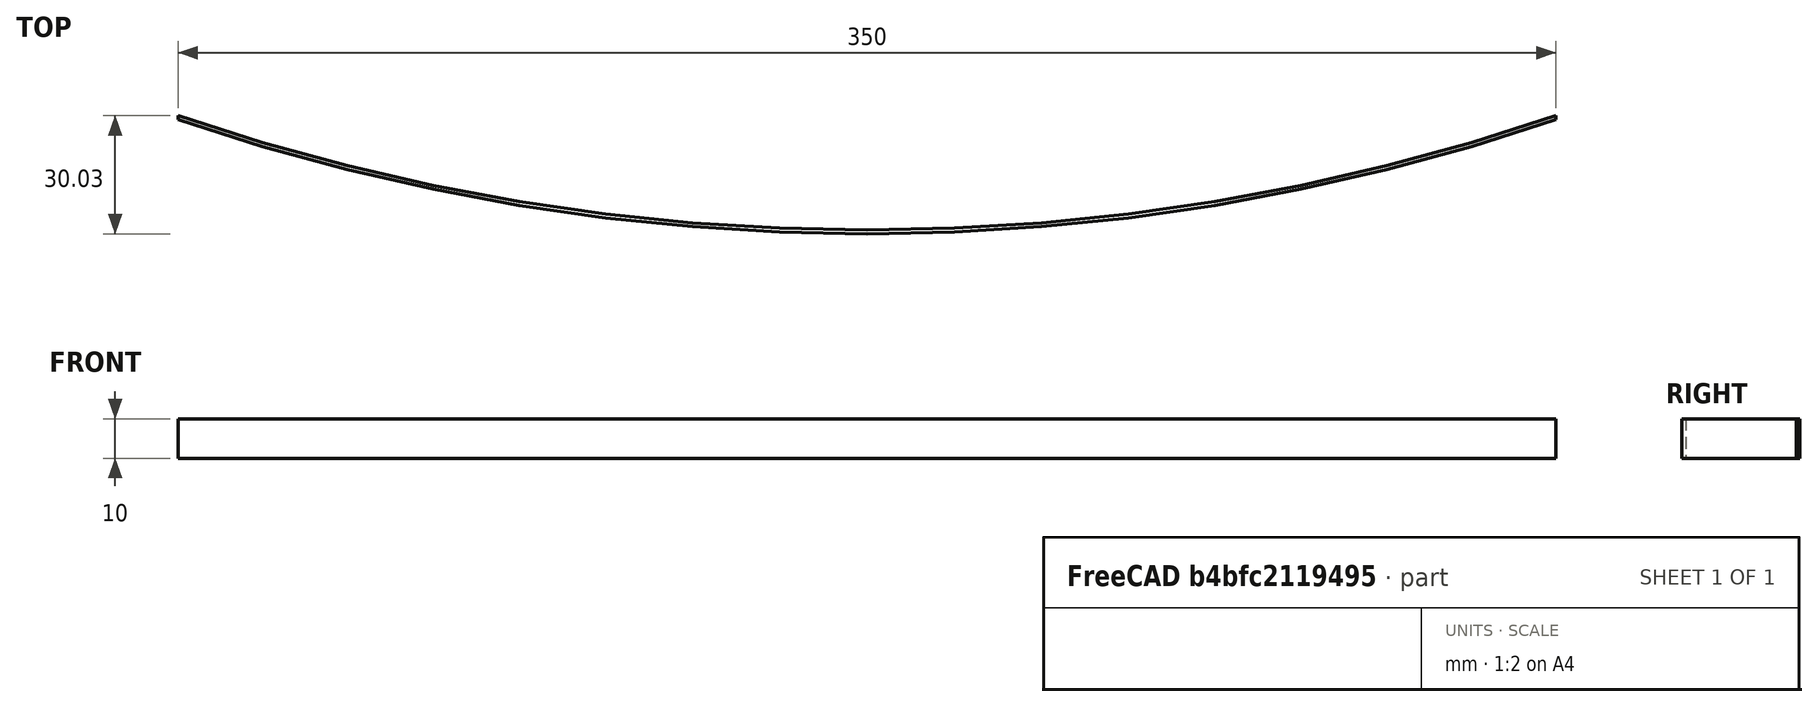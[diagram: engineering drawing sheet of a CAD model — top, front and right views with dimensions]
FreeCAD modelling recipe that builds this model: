
FCSTD DOCUMENT  (FreeCAD 0.19R24276 (Git))
Label: Strip_1
License: All rights reserved
LicenseURL: http://en.wikipedia.org/wiki/All_rights_reserved
objects: Sketcher::SketchObject×1, PartDesign::Pad×1, PartDesign::Body×1
note: 4 computed .brp shape members not serialized (recipe doc carries the construction recipe); baked Part::Feature solids carry a one-line shape summary decoded from their .brp

FEATURE [Sketcher::SketchObject] Sketch
  FullyConstrained = false
  MapMode = 5
  Support = -> [XY_Plane]
  sketch-geometry (4):
    g0: ArcOfCircle CenterX=175 CenterY=512.476 CenterZ=0 NormalX=0 NormalY=0 NormalZ=1 AngleXU=0 Radius=541.532 StartAngle=4.38332 EndAngle=5.04145
    g1: ArcOfCircle CenterX=175 CenterY=511.991 CenterZ=0 NormalX=0 NormalY=0 NormalZ=1 AngleXU=0 Radius=542.019 StartAngle=4.38363 EndAngle=5.04115
    g2: LineSegment StartX=350 StartY=-1.00002 StartZ=0 EndX=350 EndY=0 EndZ=0
    g3: LineSegment StartX=5.68e-14 StartY=1.137e-13 StartZ=0 EndX=5.68e-14 EndY=-1.00002 EndZ=0
  constraints (5):
    c: Coincident(g2,g1)
    c: Vertical(g2)
    c: Coincident(g3,g0)
    c: Coincident(g3,g1)
    c: Vertical(g3)
FEATURE [PartDesign::Pad] Pad
  Direction = (1,1,1)
  Length = 10
  Length2 = 100
  Profile = -> Sketch
  Type = 0
FEATURE [PartDesign::Body] Body
  Group = -> [Sketch,Pad]
  Origin = -> Origin
  Tip = -> Pad
